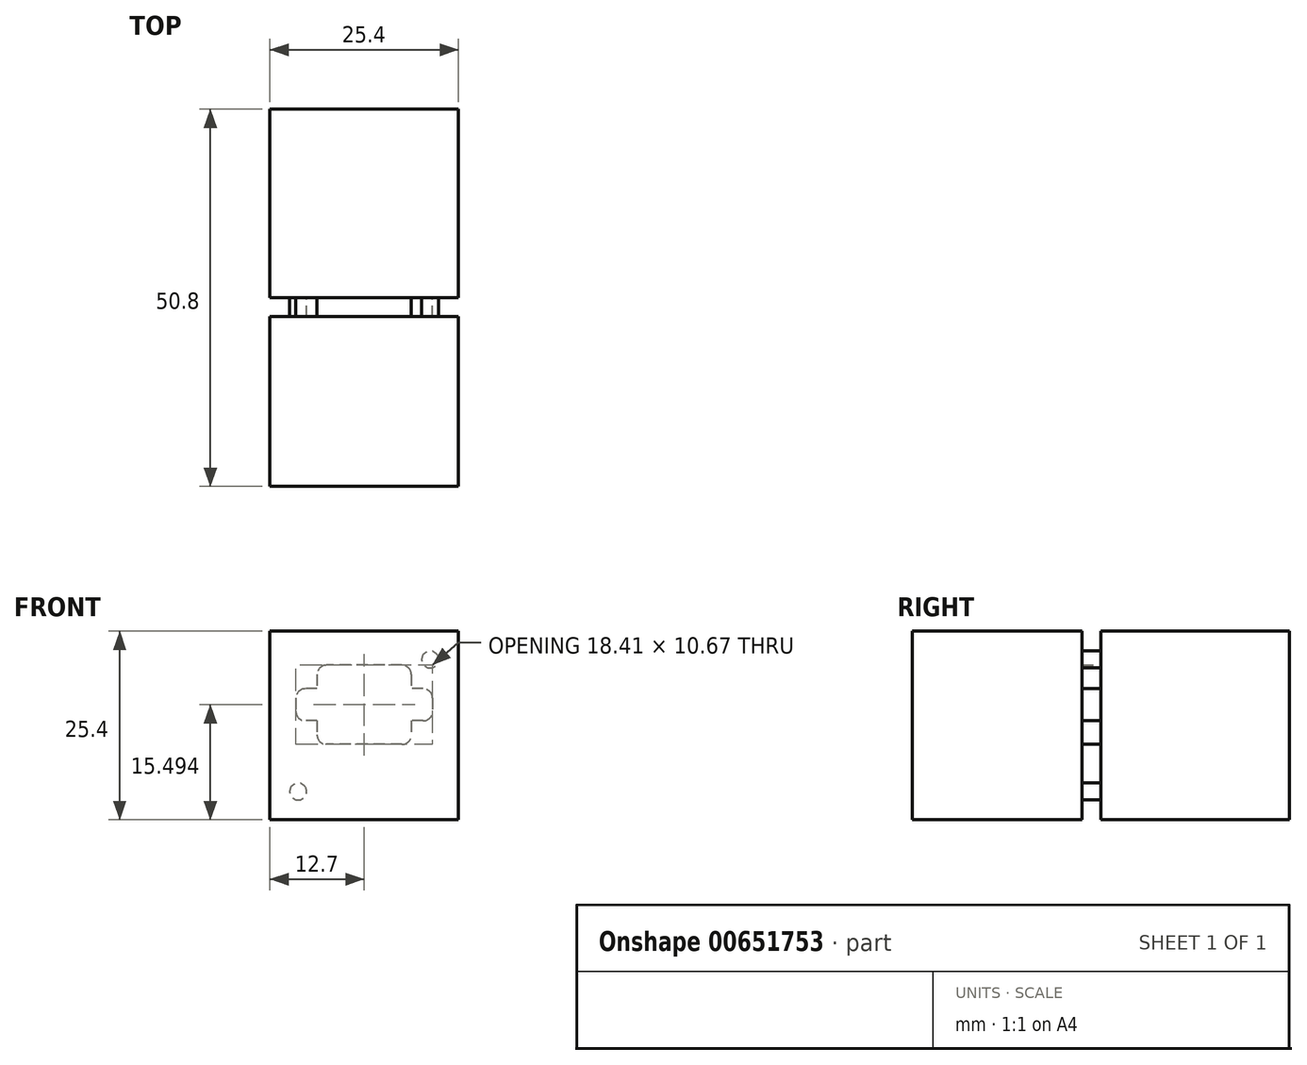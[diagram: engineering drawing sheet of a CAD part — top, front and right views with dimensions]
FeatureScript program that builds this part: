
annotation { "Feature Type Name" : "Feature", "Feature Type Description" : "" }
export const myFeature = defineFeature(function(context is Context, id is Id, definition is map)
    precondition{}
    {
        {
            var Q0;
            Q0=qCreatedBy(makeId("Front.planeOp"),FACE);
            var sketch = newSketch(context, id + "F0", { "sketchPlane" : qUnion([Q0])});
            skLineSegment(sketch, "E0.bottom", {"start": v(12.7, 12.7) * mm, "end": v(-12.7, 12.7) * mm});
            skLineSegment(sketch, "E0.top", {"start": v(12.7, -12.7) * mm, "end": v(-12.7, -12.7) * mm});
            skLineSegment(sketch, "E0.left", {"start": v(12.7, 12.7) * mm, "end": v(12.7, -12.7) * mm});
            skLineSegment(sketch, "E0.right", {"start": v(-12.7, 12.7) * mm, "end": v(-12.7, -12.7) * mm});
            skPoint(sketch, "E0.middle", {"position": v(0, 0) * mm});
            skLineSegment(sketch, "E1.bottom", {"start": v(8.9, 8.9) * mm, "end": v(-8.9, 8.9) * mm});
            skLineSegment(sketch, "E1.top", {"start": v(8.89, -8.9) * mm, "end": v(-8.9, -8.9) * mm});
            skLineSegment(sketch, "E1.left", {"start": v(8.9, 8.9) * mm, "end": v(8.9, -8.9) * mm});
            skLineSegment(sketch, "E1.right", {"start": v(-8.9, 8.9) * mm, "end": v(-8.9, -8.9) * mm});
            skLineSegment(sketch, "E2.bottom", {"start": v(5.08, 8.13) * mm, "end": v(-5.08, 8.13) * mm});
            skLineSegment(sketch, "E2.top", {"start": v(5.08, -2.54) * mm, "end": v(-5.08, -2.54) * mm});
            skLineSegment(sketch, "E2.left", {"start": v(6.35, 6.86) * mm, "end": v(6.35, -1.27) * mm});
            skLineSegment(sketch, "E2.right", {"start": v(-6.35, 6.86) * mm, "end": v(-6.35, -1.27) * mm});
            skPoint(sketch, "E2.middle", {"position": v(0, 2.8) * mm});
            skPoint(sketch, "E2.middle.positionSnap0", {"position": v(0, 12.7) * mm});
            skPoint(sketch, "E2.centerSnap0", {"position": v(0, 12.7) * mm});
            skLineSegment(sketch, "E3.bottom", {"start": v(7.94, 4.95) * mm, "end": v(-7.94, 4.95) * mm});
            skLineSegment(sketch, "E3.top", {"start": v(7.94, 0.64) * mm, "end": v(-7.94, 0.64) * mm});
            skLineSegment(sketch, "E3.left", {"start": v(9.2, 3.68) * mm, "end": v(9.2, 1.9) * mm});
            skLineSegment(sketch, "E3.right", {"start": v(-9.2, 3.68) * mm, "end": v(-9.2, 1.9) * mm});
            skPoint(sketch, "E4.visualSharp", {"position": v(-6.35, 8.13) * mm});
            skArc(sketch, "E4.filletArc", {"start": v(-5.08, 8.13) * mm, "mid": v(-5.98, 7.76) * mm, "end": v(-6.35, 6.86) * mm});
            skPoint(sketch, "E5.visualSharp", {"position": v(6.35, 8.13) * mm});
            skArc(sketch, "E5.filletArc", {"start": v(6.35, 6.86) * mm, "mid": v(5.98, 7.76) * mm, "end": v(5.08, 8.13) * mm});
            skPoint(sketch, "E6.visualSharp", {"position": v(6.35, -2.54) * mm});
            skArc(sketch, "E6.filletArc", {"start": v(5.08, -2.54) * mm, "mid": v(5.98, -2.17) * mm, "end": v(6.35, -1.27) * mm});
            skPoint(sketch, "E7.visualSharp", {"position": v(-6.35, -2.54) * mm});
            skArc(sketch, "E7.filletArc", {"start": v(-6.35, -1.27) * mm, "mid": v(-5.98, -2.17) * mm, "end": v(-5.08, -2.54) * mm});
            skPoint(sketch, "E8.visualSharp", {"position": v(-9.2, 0.64) * mm});
            skArc(sketch, "E8.filletArc", {"start": v(-9.2, 1.9) * mm, "mid": v(-8.84, 1) * mm, "end": v(-7.94, 0.64) * mm});
            skPoint(sketch, "E9.visualSharp", {"position": v(-9.2, 4.95) * mm});
            skArc(sketch, "E9.filletArc", {"start": v(-7.94, 4.95) * mm, "mid": v(-8.84, 4.58) * mm, "end": v(-9.2, 3.68) * mm});
            skPoint(sketch, "E10.visualSharp", {"position": v(9.2, 4.95) * mm});
            skArc(sketch, "E10.filletArc", {"start": v(9.2, 3.68) * mm, "mid": v(8.84, 4.58) * mm, "end": v(7.94, 4.95) * mm});
            skPoint(sketch, "E11.visualSharp", {"position": v(9.2, 0.64) * mm});
            skArc(sketch, "E11.filletArc", {"start": v(7.94, 0.63) * mm, "mid": v(8.84, 1) * mm, "end": v(9.2, 1.9) * mm});
            skPoint(sketch, "E12", {"position": v(-6.35, 4.95) * mm});
            skPoint(sketch, "E13", {"position": v(-6.35, 0.64) * mm});
            skPoint(sketch, "E14", {"position": v(6.35, 0.64) * mm});
            skPoint(sketch, "E15", {"position": v(6.35, 4.95) * mm});
            skCircle(sketch, "E16", {"center": v(8.9, 8.9) * mm, "radius": 1.14 * mm});
            skCircle(sketch, "E17", {"center": v(-8.9, -8.9) * mm, "radius": 1.14 * mm});
            skSolve(sketch);
        }
        {
            var Q0;
            Q0=makeQuery(id+"F0.imprint","IMPRINT",FACE,{"disambiguationData":[TD([[makeQuery(id+"F0.imprint","IMPRINT",EDGE,{"derivedFrom":sQuery(id+"F0.wireOp",EDGE,"E0.bottom")}),1.0]])]});
            var Q1;
            Q1=makeQuery(id+"F0.imprint","IMPRINT",FACE,{"disambiguationData":[TD([[makeQuery(id+"F0.imprint","IMPRINT",EDGE,{"derivedFrom":sQuery(id+"F0.wireOp",EDGE,"E2.top")}),1.0]])]});
            var Q2;
            Q2=makeQuery(id+"F0.imprint","IMPRINT",FACE,{"disambiguationData":[TD([[makeQuery(id+"F0.imprint","IMPRINT",EDGE,{"derivedFrom":sQuery(id+"F0.wireOp",EDGE,"E2.bottom")}),-1.0]])]});
            var Q3;
            {var subQ0=sQuery(id+"F0.wireOp",EDGE,"E1.left");var subQ1=sQuery(id+"F0.wireOp",EDGE,"E1.bottom");var subQ2=makeQuery(id+"F0.imprint","INTERSECT",VERTEX,{"derivedFrom":[subQ1,subQ0]});Q3=makeQuery(id+"F0.imprint","IMPRINT",FACE,{"disambiguationData":[TD([[makeQuery(id+"F0.imprint","IMPRINT",EDGE,{"disambiguationData":[TD([[subQ2,-1.0]])],"derivedFrom":subQ1}),1.0]])]});}
            var Q4;
            {var subQ0=sQuery(id+"F0.wireOp",EDGE,"E1.left");var subQ1=sQuery(id+"F0.wireOp",EDGE,"E1.bottom");var subQ2=makeQuery(id+"F0.imprint","INTERSECT",VERTEX,{"derivedFrom":[subQ1,subQ0]});Q4=makeQuery(id+"F0.imprint","IMPRINT",FACE,{"disambiguationData":[TD([[makeQuery(id+"F0.imprint","IMPRINT",EDGE,{"disambiguationData":[TD([[subQ2,-1.0]])],"derivedFrom":subQ1}),-1.0]])]});}
            var Q5;
            {var subQ0=sQuery(id+"F0.wireOp",EDGE,"E1.right");var subQ1=sQuery(id+"F0.wireOp",EDGE,"E1.top");var subQ2=makeQuery(id+"F0.imprint","INTERSECT",VERTEX,{"derivedFrom":[subQ1,subQ0]});Q5=makeQuery(id+"F0.imprint","IMPRINT",FACE,{"disambiguationData":[TD([[makeQuery(id+"F0.imprint","IMPRINT",EDGE,{"disambiguationData":[TD([[subQ2,1.0]])],"derivedFrom":subQ1}),-1.0]])]});}
            var Q6;
            {var subQ0=sQuery(id+"F0.wireOp",EDGE,"E1.right");var subQ1=sQuery(id+"F0.wireOp",EDGE,"E1.top");var subQ2=makeQuery(id+"F0.imprint","INTERSECT",VERTEX,{"derivedFrom":[subQ1,subQ0]});Q6=makeQuery(id+"F0.imprint","IMPRINT",FACE,{"disambiguationData":[TD([[makeQuery(id+"F0.imprint","IMPRINT",EDGE,{"disambiguationData":[TD([[subQ2,1.0]])],"derivedFrom":subQ1}),1.0]])]});}
            var Q7;
            {var subQ0=sQuery(id+"F0.wireOp",EDGE,"E3.bottom");var subQ1=sQuery(id+"F0.wireOp",EDGE,"E2.left");var subQ2=makeQuery(id+"F0.imprint","INTERSECT",VERTEX,{"derivedFrom":[subQ1,subQ0]});Q7=makeQuery(id+"F0.imprint","IMPRINT",FACE,{"disambiguationData":[TD([[makeQuery(id+"F0.imprint","IMPRINT",EDGE,{"disambiguationData":[TD([[subQ2,-1.0]])],"derivedFrom":subQ1}),-1.0]])]});}
            var Q8;
            {var subQ5=sQuery(id+"F0.wireOp",EDGE,"E9.filletArc");var subQ9=sQuery(id+"F0.wireOp",EDGE,"E1.right");var subQ11=makeQuery(id+"F0.imprint","INTERSECT",VERTEX,{"derivedFrom":[subQ9,subQ5]});Q8=makeQuery(id+"F0.imprint","IMPRINT",FACE,{"disambiguationData":[TD([[makeQuery(id+"F0.imprint","IMPRINT",EDGE,{"disambiguationData":[TD([[subQ11,-1.0]])],"derivedFrom":subQ9}),1.0]])]});}
            var Q9;
            {var subQ5=sQuery(id+"F0.wireOp",EDGE,"E10.filletArc");var subQ9=sQuery(id+"F0.wireOp",EDGE,"E1.left");var subQ10=makeQuery(id+"F0.imprint","INTERSECT",VERTEX,{"derivedFrom":[subQ9,subQ5]});Q9=makeQuery(id+"F0.imprint","IMPRINT",FACE,{"disambiguationData":[TD([[makeQuery(id+"F0.imprint","IMPRINT",EDGE,{"disambiguationData":[TD([[subQ10,-1.0]])],"derivedFrom":subQ9}),-1.0]])]});}
            var Q10;
            {var subQ5=sQuery(id+"F0.wireOp",EDGE,"E3.left");Q10=makeQuery(id+"F0.imprint","IMPRINT",FACE,{"disambiguationData":[TD([[makeQuery(id+"F0.imprint","IMPRINT",EDGE,{"derivedFrom":subQ5}),-1.0]])]});}
            var Q11;
            Q11=makeQuery(id+"F0.imprint","IMPRINT",FACE,{"disambiguationData":[TD([[makeQuery(id+"F0.imprint","IMPRINT",EDGE,{"derivedFrom":sQuery(id+"F0.wireOp",EDGE,"E2.top")}),-1.0]])]});
            var Q12;
            Q12=makeQuery(id+"F0.imprint","IMPRINT",FACE,{"disambiguationData":[TD([[makeQuery(id+"F0.imprint","IMPRINT",EDGE,{"derivedFrom":sQuery(id+"F0.wireOp",EDGE,"E2.bottom")}),1.0]])]});
            var Q13;
            {var subQ5=sQuery(id+"F0.wireOp",EDGE,"E3.right");Q13=makeQuery(id+"F0.imprint","IMPRINT",FACE,{"disambiguationData":[TD([[makeQuery(id+"F0.imprint","IMPRINT",EDGE,{"derivedFrom":subQ5}),1.0]])]});}
            extrude(context, id + "F1", {"entities" : qUnion([Q0, Q1, Q2, Q3, Q4, Q5, Q6, Q7, Q8, Q9, Q10, Q11, Q12, Q13]), "oppositeDirection" : true, "depth" : 25.4 * mm, "offsetDistance" : 25.4 * mm, "hasSecondDirection" : true, "secondDirectionOppositeDirection" : false, "secondDirectionDepth" : 25.4 * mm});
        }
        {
            var Q0;
            Q0=makeQuery(id+"F0.imprint","IMPRINT",FACE,{"disambiguationData":[TD([[makeQuery(id+"F0.imprint","IMPRINT",EDGE,{"derivedFrom":sQuery(id+"F0.wireOp",EDGE,"E0.bottom")}),1.0]])]});
            var Q1;
            Q1=makeQuery(id+"F0.imprint","IMPRINT",FACE,{"disambiguationData":[TD([[makeQuery(id+"F0.imprint","IMPRINT",EDGE,{"derivedFrom":sQuery(id+"F0.wireOp",EDGE,"E2.bottom")}),-1.0]])]});
            var Q2;
            Q2=makeQuery(id+"F0.imprint","IMPRINT",FACE,{"disambiguationData":[TD([[makeQuery(id+"F0.imprint","IMPRINT",EDGE,{"derivedFrom":sQuery(id+"F0.wireOp",EDGE,"E2.top")}),1.0]])]});
            extrude(context, id + "F2", {"entities" : qUnion([Q0, Q1, Q2]), "operationType" : NewBodyOperationType.REMOVE, "depth" : 2.54 * mm, "offsetDistance" : 25.4 * mm});
        }
    });
